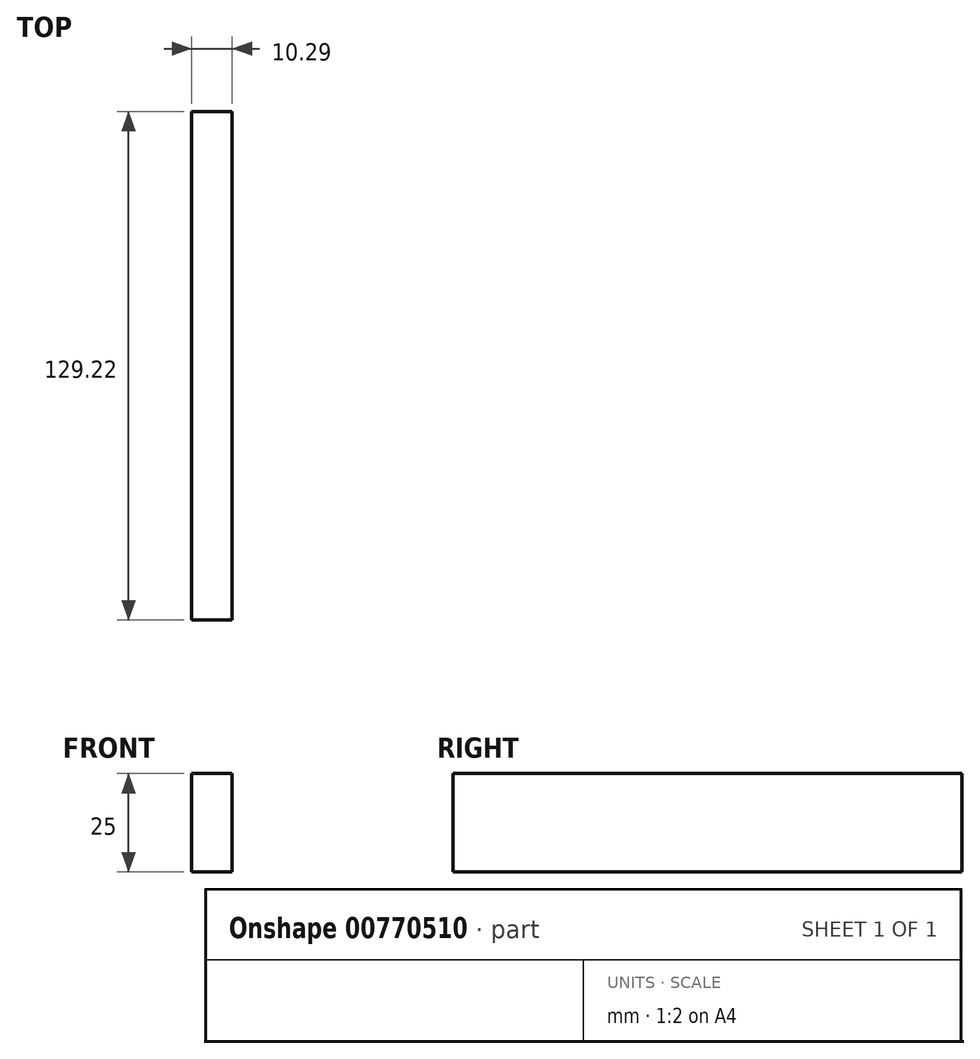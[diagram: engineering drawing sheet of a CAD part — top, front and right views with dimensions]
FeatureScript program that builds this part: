
annotation { "Feature Type Name" : "Feature", "Feature Type Description" : "" }
export const myFeature = defineFeature(function(context is Context, id is Id, definition is map)
    precondition{}
    {
        {
            var Q0;
            Q0=qCreatedBy(makeId("Top.planeOp"),FACE);
            var sketch = newSketch(context, id + "F0", { "sketchPlane" : qUnion([Q0])});
            skLineSegment(sketch, "E0.bottom", {"start": v(-36.3, -74.28) * mm, "end": v(-46.58, -74.28) * mm});
            skLineSegment(sketch, "E0.top", {"start": v(-36.3, 54.94) * mm, "end": v(-46.58, 54.94) * mm});
            skLineSegment(sketch, "E0.left", {"start": v(-36.3, -74.28) * mm, "end": v(-36.3, 54.94) * mm});
            skLineSegment(sketch, "E0.right", {"start": v(-46.58, -74.28) * mm, "end": v(-46.58, 54.94) * mm});
            skSolve(sketch);
        }
        {
            var Q0;
            Q0=makeQuery(id+"F0.imprint","IMPRINT",FACE,{"disambiguationData":[TD([[makeQuery(id+"F0.imprint","IMPRINT",EDGE,{"derivedFrom":sQuery(id+"F0.wireOp",EDGE,"E0.bottom")}),-1.0]])]});
            extrude(context, id + "F1", {"entities" : qUnion([Q0]), "depth" : 25 * mm, "offsetDistance" : 25 * mm});
        }
    });
